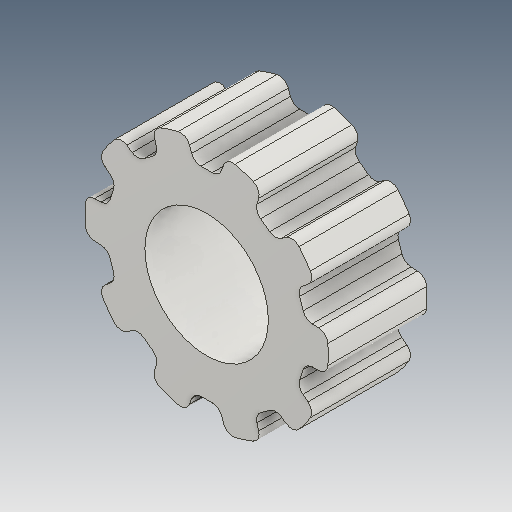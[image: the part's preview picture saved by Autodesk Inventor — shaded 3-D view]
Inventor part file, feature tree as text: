
AUTODESK INVENTOR PART (.ipt)
format: ipt  version: 2020.3 (Build 243373010, 373A)  size: 241,664 bytes
history: native  units: mm (DEFAULTED — no unit token found)
features: other x3, extrude x3, fillet x1, pattern_circular x1, sketch x1
ambient origin geometry x8: Origin, YZ Plane, XZ Plane, XY Plane, X Axis, Y Axis, Z Axis, Center Point
bodies: Solid1 (feature_tree)
feature tree (9):
  other  "Pulley Sketch"
  extrude  "Base Body"  Depth=1.1684mm
  extrude  "Tooth"  Depth=1.1684mm
  fillet  "Tooth Fillet"  Radius=6.981317mm
  pattern_circular  "Teeth"  [2 undecoded]
  other  "Left flange"
  other  "Right flange"
  extrude  "Extrusion3"  Depth=12.0mm
  sketch  "Sketch2"  dims[d0=30.319017mm d1=0.381mm d2=2.667mm d3=6.981317mm d4=3.048mm d5=12.0mm d6=0.0mm d7=12.0mm d8=0.0mm d9=1.1938mm d10=1.1684mm d11=100.0mm d12=360.0deg d15=0.0mm d16=0.0mm d17=15.0mm d18=0.0mm d19=0.0mm]
note: 2 required parameter values undecoded (feature->parameter linkage not recoverable at this tier; creation-order binding heuristic only, values carry confidence <= 0.55)
